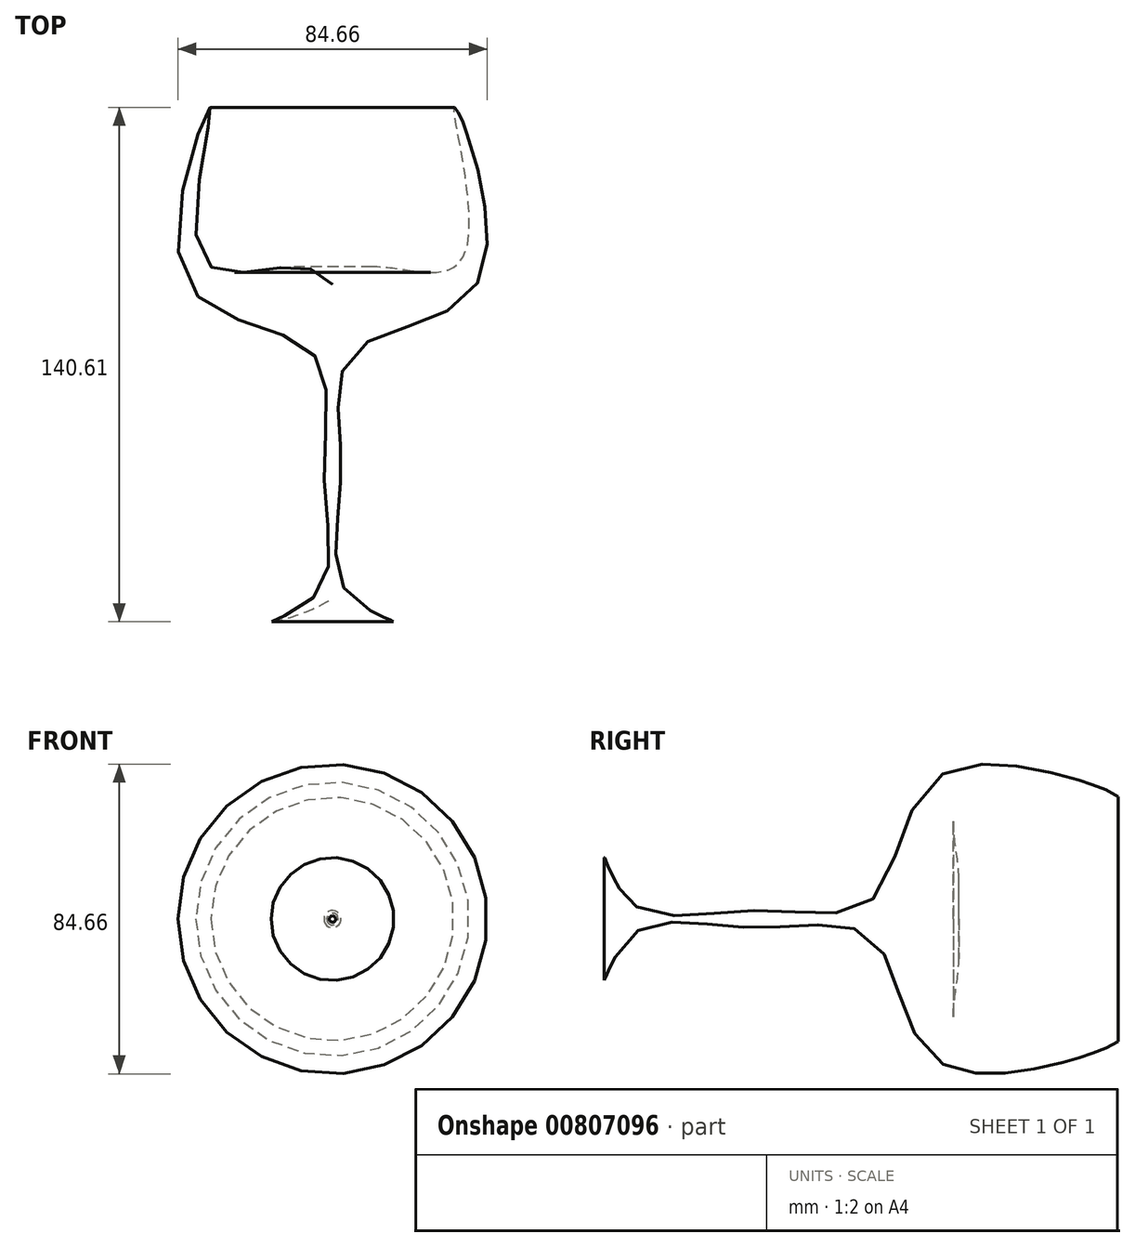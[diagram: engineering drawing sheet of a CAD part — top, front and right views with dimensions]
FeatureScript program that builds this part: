
annotation { "Feature Type Name" : "Feature", "Feature Type Description" : "" }
export const myFeature = defineFeature(function(context is Context, id is Id, definition is map)
    precondition{}
    {
        {
            var Q0;
            Q0=qCreatedBy(makeId("Top.planeOp"),FACE);
            var sketch = newSketch(context, id + "F0", { "sketchPlane" : qUnion([Q0])});
            skFitSpline(sketch, "E0", {"points": [v(-33.37, 66.44) * mm, v(-40.7, 20.6) * mm, v(-6.16, 0) * mm, v(-2.32, -33.14) * mm, v(-4.34, -66.62) * mm, v(-16.8, -74.13) * mm, v(3.43, -65.13) * mm, v(6.71, -26.27) * mm, v(0, 18.03) * mm, v(-15.14, 22.58) * mm, v(-36.1, 26.2) * mm, v(-33.37, 66.44) * mm]});
            skLineSegment(sketch, "E1", {"start": v(0, 75.8) * mm, "end": v(0, -87.1) * mm});
            skSolve(sketch);
        }
        {
            var Q0;
            {var subQ0=sQuery(id+"F0.wireOp",EDGE,"E1");var subQ1=sQuery(id+"F0.wireOp",EDGE,"E0");var subQ2=makeQuery(id+"F0.imprint","INTERSECT",VERTEX,{"disambiguationData":[OD(0.0)],"derivedFrom":[subQ1,subQ0]});Q0=makeQuery(id+"F0.imprint","IMPRINT",FACE,{"disambiguationData":[TD([[makeQuery(id+"F0.imprint","IMPRINT",EDGE,{"disambiguationData":[TD([[subQ2,1.0]])],"derivedFrom":subQ1}),1.0]])]});}
            var Q1;
            Q1=sQuery(id+"F0.wireOp",EDGE,"E1");
            revolve(context, id + "F1", {"surfaceOperationType" : NewSurfaceOperationType.NEW, "entities" : qUnion([Q0]), "axis" : qUnion([Q1]), "revolveType" : RevolveType.FULL});
        }
    });
